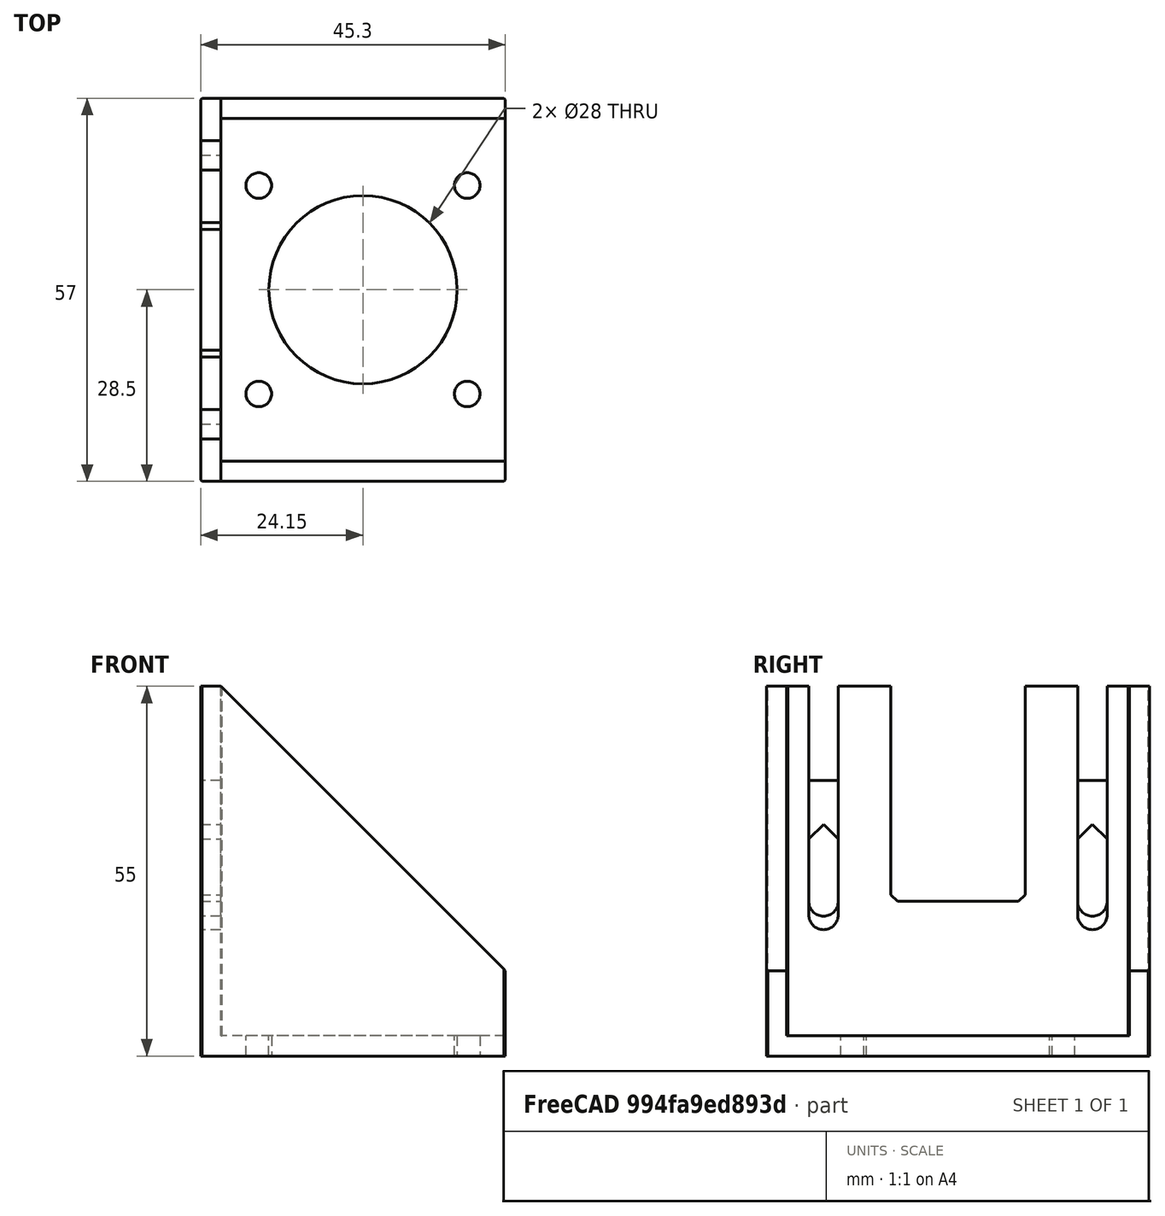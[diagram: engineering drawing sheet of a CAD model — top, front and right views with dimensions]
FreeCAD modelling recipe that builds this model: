
FCSTD DOCUMENT  (FreeCAD 0.17R13522 (Git))
Label: motor_holder17_40boltsep_rail2_v02
License: All rights reserved
LicenseURL: http://en.wikipedia.org/wiki/All_rights_reserved
objects: Part::Feature×3, Part::Box×3, Part::Cut×3, Part::Chamfer×1, Part::MultiFuse×1
note: 11 computed .brp shape members not serialized (recipe doc carries the construction recipe); baked Part::Feature solids carry a one-line shape summary decoded from their .brp

FEATURE [Part::Feature] nema_holder
  shape: bbox 45.3 x 57 x 55 mm, 31 faces (baked)
FEATURE [Part::Box] Box  label="Cube"
  AttacherType = Attacher::AttachEngine3D
  Height = 33
  Length = 5
  Placement = pos=(-25,-10,20) rot=(0,0,1;0rad)
  Width = 20
FEATURE [Part::Chamfer] Chamfer
  Base = -> Box
  Edges = 2 edges r=1: [Edge9,Edge11]
FEATURE [Part::Cut] Cut
  Base = -> nema_holder
  Refine = true
  Tool = -> Chamfer
FEATURE [Part::Feature] nema_holder001
  shape: bbox 45.3 x 57 x 55 mm, 31 faces (baked)
FEATURE [Part::Cut] Cut001
  Base = -> nema_holder001
  Refine = true
  Tool = -> Chamfer
FEATURE [Part::Box] Box001  label="Cube001"
  AttacherType = Attacher::AttachEngine3D
  Height = 10
  Length = 3
  Placement = pos=(0,-5,0) rot=(0,0,1;0rad)
  Width = 10
FEATURE [Part::Box] Box002  label="Cube002"
  AttacherType = Attacher::AttachEngine3D
  Height = 6
  Length = 5
  Placement = pos=(-1,0,-5) rot=(1,0,0;0.785398rad)
  Width = 6
FEATURE [Part::Cut] Cut002
  Base = -> Box001
  Placement = pos=(-24.15,20,28) rot=(0,0,1;0rad)
  Refine = true
  Tool = -> Box002
FEATURE [Part::Feature] Cut002001  label="Cut003"
  Placement = pos=(-24.15,-20,28) rot=(0,0,1;0rad)
  shape: bbox 3 x 10 x 10 mm, 9 faces (baked)
FEATURE [Part::MultiFuse] Fusion  label="motor_holder"
  Refine = true
  Shapes = -> [Cut001,Cut002,Cut002001]
